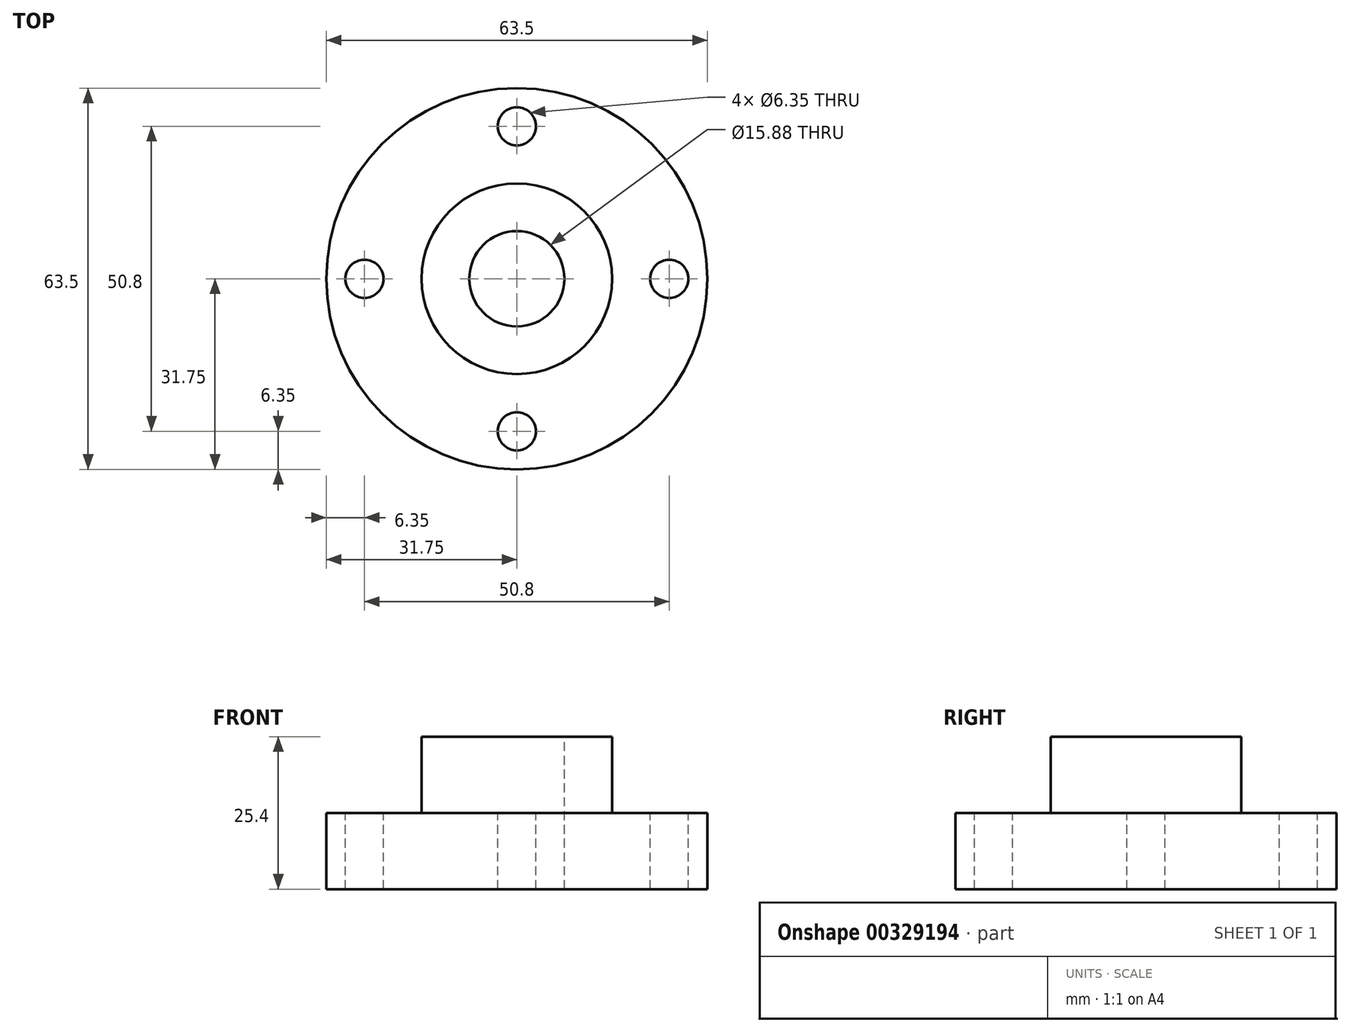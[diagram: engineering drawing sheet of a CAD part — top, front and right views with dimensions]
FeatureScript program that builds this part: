
annotation { "Feature Type Name" : "Feature", "Feature Type Description" : "" }
export const myFeature = defineFeature(function(context is Context, id is Id, definition is map)
    precondition{}
    {
        {
            var Q0;
            Q0=qCreatedBy(makeId("Top.planeOp"),FACE);
            var sketch = newSketch(context, id + "F0", { "sketchPlane" : qUnion([Q0])});
            skCircle(sketch, "E0", {"center": v(0, 0) * mm, "radius": 31.75 * mm});
            skSolve(sketch);
        }
        {
            var Q0;
            Q0 = qSketchRegion(id + "F0", true);
            extrude(context, id + "F1", {"entities" : qUnion([Q0]), "depth" : 25.4 * mm});
        }
        {
            var Q0;
            Q0=makeQuery(id+"F1.opExtrude","CAP_FACE",FACE,{"disambiguationData":[OSD([sQuery(id+"F0.wireOp",EDGE,"E0")])],"isStart":false});
            var sketch = newSketch(context, id + "F2", { "sketchPlane" : qUnion([Q0])});
            skCircle(sketch, "E1", {"center": v(0, 0) * mm, "radius": 31.75 * mm});
            skCircle(sketch, "E2", {"center": v(0, 0) * mm, "radius": 15.88 * mm});
            skSolve(sketch);
        }
        {
            var Q0;
            Q0 = qSketchRegion(id + "F2", true);
            extrude(context, id + "F3", {"entities" : qUnion([Q0]), "operationType" : NewBodyOperationType.REMOVE, "oppositeDirection" : true, "depth" : 12.7 * mm});
        }
        {
            var Q0;
            Q0=makeQuery(id+"F1.opExtrude","CAP_FACE",FACE,{"disambiguationData":[OSD([sQuery(id+"F0.wireOp",EDGE,"E0")])],"isStart":false});
            var sketch = newSketch(context, id + "F4", { "sketchPlane" : qUnion([Q0])});
            skCircle(sketch, "E3", {"center": v(0, 0) * mm, "radius": 7.94 * mm});
            skCircle(sketch, "E4", {"center": v(0, 25.4) * mm, "radius": 3.18 * mm});
            skCircle(sketch, "E5", {"center": v(0, -25.4) * mm, "radius": 3.18 * mm});
            skCircle(sketch, "E6", {"center": v(25.4, 0) * mm, "radius": 3.18 * mm});
            skCircle(sketch, "E7", {"center": v(-25.4, 0) * mm, "radius": 3.18 * mm});
            skSolve(sketch);
        }
        {
            var Q0;
            Q0 = qSketchRegion(id + "F4", true);
            extrude(context, id + "F5", {"entities" : qUnion([Q0]), "operationType" : NewBodyOperationType.REMOVE, "endBound" : BoundingType.THROUGH_ALL, "oppositeDirection" : true, "depth" : 25.4 * mm});
        }
    });
